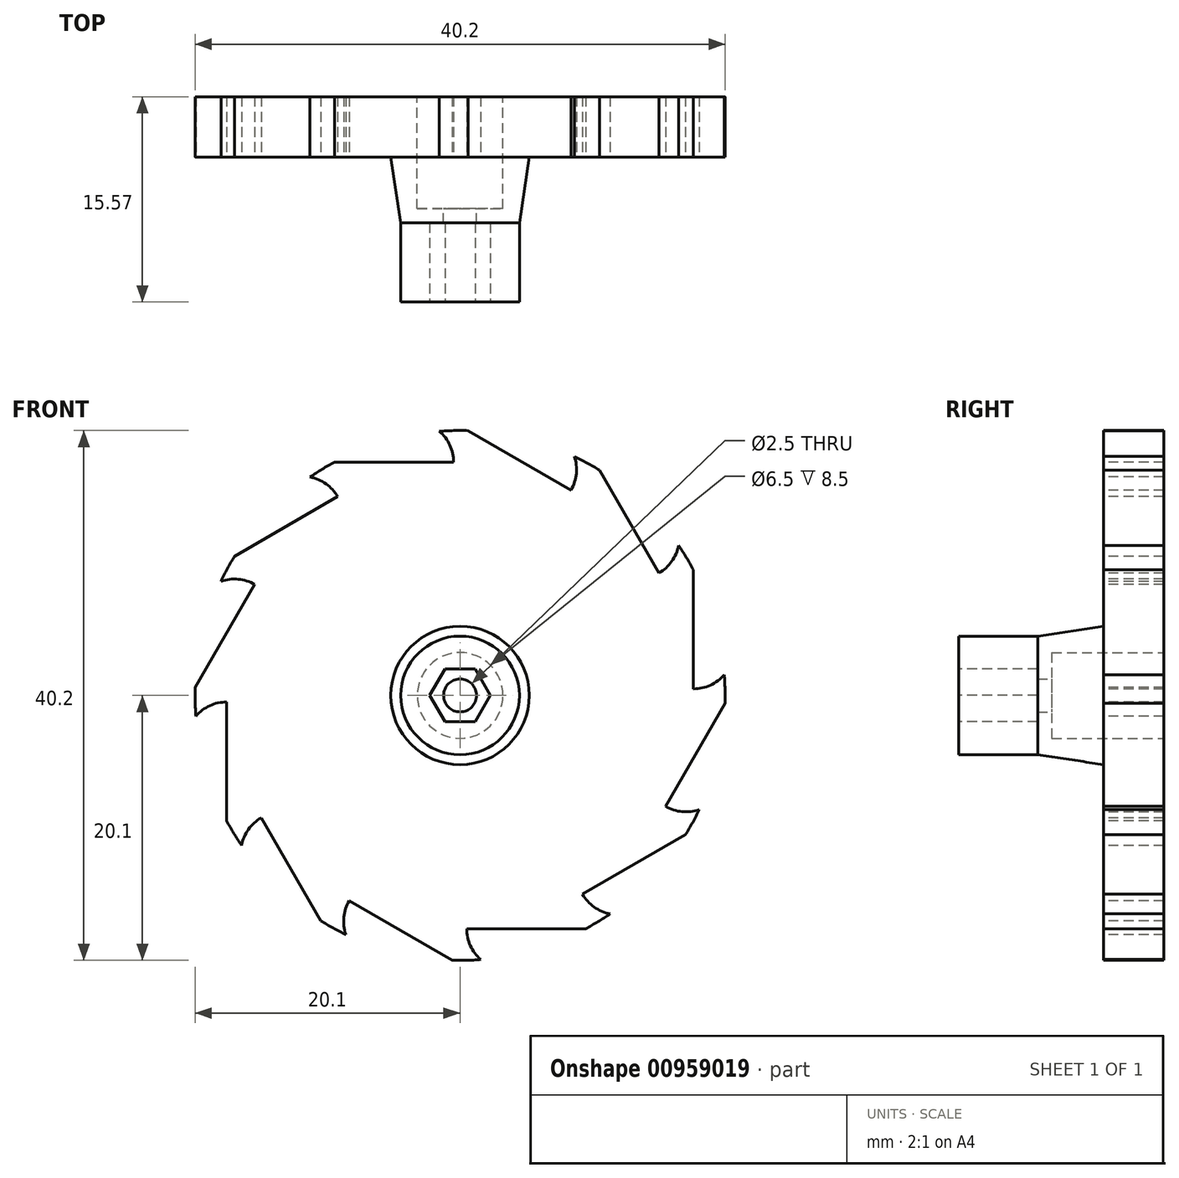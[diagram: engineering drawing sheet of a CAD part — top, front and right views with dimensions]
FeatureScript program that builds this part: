
annotation { "Feature Type Name" : "Feature", "Feature Type Description" : "" }
export const myFeature = defineFeature(function(context is Context, id is Id, definition is map)
    precondition{}
    {
        {
            var Q0;
            Q0=qCreatedBy(makeId("Front.planeOp"),FACE);
            var sketch = newSketch(context, id + "F0", { "sketchPlane" : qUnion([Q0])});
            skCircle(sketch, "E0", {"center": v(0, 0) * mm, "radius": 20.1 * mm});
            skSolve(sketch);
        }
        {
            var Q0;
            Q0=makeQuery(id+"F0.imprint","IMPRINT",FACE,{"disambiguationData":[TD([[makeQuery(id+"F0.imprint","IMPRINT",EDGE,{"derivedFrom":sQuery(id+"F0.wireOp",EDGE,"E0")}),1.0]])]});
            extrude(context, id + "F1", {"entities" : qUnion([Q0]), "depth" : 4.57 * mm, "offsetDistance" : 25.4 * mm});
        }
        {
            var Q0;
            Q0=makeQuery(id+"F1.opExtrude","CAP_FACE",FACE,{"disambiguationData":[OSD([sQuery(id+"F0.wireOp",EDGE,"E0")])],"isStart":false});
            var sketch = newSketch(context, id + "F2", { "sketchPlane" : qUnion([Q0])});
            skLineSegment(sketch, "E1", {"start": v(0, 20.1) * mm, "end": v(0, -20.1) * mm});
            skLineSegment(sketch, "E2", {"start": v(-9.53, 17.7) * mm, "end": v(9.53, 17.7) * mm});
            skArc(sketch, "E3", {"start": v(1.57, 20.04) * mm, "mid": v(0.78, 18.99) * mm, "end": v(0.5, 17.7) * mm});
            skArc(sketch, "E4.MirrorCS", {"start": v(-1.57, 20.04) * mm, "mid": v(-0.78, 18.99) * mm, "end": v(-0.5, 17.7) * mm});
            skArc(sketch, "E5", {"start": v(1.57, 20.04) * mm, "mid": v(0, 20.1) * mm, "end": v(-1.57, 20.04) * mm});
            skPoint(sketch, "E6.orphan", {"position": v(6.66, 17.7) * mm});
            skPoint(sketch, "E7.orphan", {"position": v(-6.66, 17.7) * mm});
            skSolve(sketch);
        }
        {
            var Q0;
            {var subQ5=sQuery(id+"F2.wireOp",EDGE,"E4.MirrorCS");Q0=makeQuery(id+"F2.imprint","IMPRINT",FACE,{"disambiguationData":[TD([[makeQuery(id+"F2.imprint","IMPRINT",EDGE,{"derivedFrom":subQ5}),1.0]])]});}
            var Q1;
            {var subQ5=sQuery(id+"F2.wireOp",EDGE,"E3");Q1=makeQuery(id+"F2.imprint","IMPRINT",FACE,{"disambiguationData":[TD([[makeQuery(id+"F2.imprint","IMPRINT",EDGE,{"derivedFrom":subQ5}),-1.0]])]});}
            extrude(context, id + "F3", {"entities" : qUnion([Q0, Q1]), "operationType" : NewBodyOperationType.REMOVE, "endBound" : BoundingType.THROUGH_ALL, "oppositeDirection" : true, "depth" : 25.4 * mm, "offsetDistance" : 25.4 * mm});
        }
        {
            var Q0;
            Q0=makeQuery(id+"F3.boolean.opBoolean","COPY",FACE,{"derivedFrom":makeQuery(id+"F3.opExtrude","SWEPT_FACE",FACE,{"disambiguationData":[OSD([sQuery(id+"F2.wireOp",EDGE,"E4.MirrorCS")])]})});
            var Q1;
            Q1=makeQuery(id+"F3.boolean.opBoolean","COPY",FACE,{"derivedFrom":makeQuery(id+"F3.opExtrude","SWEPT_FACE",FACE,{"disambiguationData":[OSD([sQuery(id+"F2.wireOp",EDGE,"E2")])]})});
            var Q2;
            Q2=makeQuery(id+"F3.boolean.opBoolean","COPY",FACE,{"derivedFrom":makeQuery(id+"F3.opExtrude","SWEPT_FACE",FACE,{"disambiguationData":[OSD([sQuery(id+"F2.wireOp",EDGE,"E3")])]})});
            var Q3;
            Q3=makeQuery(id+"F1.opExtrude","SWEPT_FACE",FACE,{"disambiguationData":[OSD([sQuery(id+"F0.wireOp",EDGE,"E0")])]});
            circularPattern(context, id + "F4", {"patternType" : PatternType.FACE, "faces" : qUnion([Q0, Q1, Q2]), "axis" : qUnion([Q3]), "angle" : 360 * degree, "instanceCount" : 36, "equalSpace" : true});
        }
        {
            var Q0;
            Q0=makeQuery(id+"F1.opExtrude","CAP_FACE",FACE,{"disambiguationData":[OSD([sQuery(id+"F0.wireOp",EDGE,"E0")])],"isStart":false});
            var sketch = newSketch(context, id + "F5", { "sketchPlane" : qUnion([Q0])});
            skCircle(sketch, "E8.cCircle", {"center": v(0, 0) * mm, "radius": 2 * mm, "construction": true});
            skLineSegment(sketch, "E8.0", {"start": v(-1.15, 2) * mm, "end": v(1.15, 2) * mm, "construction": true});
            skLineSegment(sketch, "E8.1", {"start": v(1.15, 2) * mm, "end": v(2.3, 0) * mm, "construction": true});
            skLineSegment(sketch, "E8.2", {"start": v(2.3, 0) * mm, "end": v(1.15, -2) * mm, "construction": true});
            skLineSegment(sketch, "E8.3", {"start": v(1.15, -2) * mm, "end": v(-1.15, -2) * mm, "construction": true});
            skLineSegment(sketch, "E8.4", {"start": v(-1.15, -2) * mm, "end": v(-2.3, 0) * mm, "construction": true});
            skLineSegment(sketch, "E8.5", {"start": v(-2.3, 0) * mm, "end": v(-1.15, 2) * mm, "construction": true});
            skPoint(sketch, "E8.0.midPoint", {"position": v(0, 2) * mm});
            skCircle(sketch, "E9", {"center": v(0, 0) * mm, "radius": 5.25 * mm});
            skSolve(sketch);
        }
        {
            var Q0;
            Q0=makeQuery(id+"F5.imprint","IMPRINT",FACE,{"disambiguationData":[TD([[makeQuery(id+"F5.imprint","IMPRINT",EDGE,{"derivedFrom":sQuery(id+"F5.wireOp",EDGE,"E9")}),-1.0]])]});
            cPlane(context, id + "F6", {"entities" : qUnion([Q0]), "cplaneType" : CPlaneType.OFFSET, "offset" : 5 * mm, "width" : 152.4 * mm, "height" : 152.4 * mm});
        }
        {
            var Q0;
            Q0=qCreatedBy(id+"F6.planeOp",FACE);
            var sketch = newSketch(context, id + "F7", { "sketchPlane" : qUnion([Q0])});
            skCircle(sketch, "E10.cCircle", {"center": v(0, 0) * mm, "radius": 2 * mm, "construction": true});
            skLineSegment(sketch, "E10.0", {"start": v(-1.15, 2) * mm, "end": v(1.15, 2) * mm, "construction": true});
            skLineSegment(sketch, "E10.1", {"start": v(1.15, 2) * mm, "end": v(2.3, 0) * mm, "construction": true});
            skLineSegment(sketch, "E10.2", {"start": v(2.3, 0) * mm, "end": v(1.15, -2) * mm, "construction": true});
            skLineSegment(sketch, "E10.3", {"start": v(1.15, -2) * mm, "end": v(-1.15, -2) * mm, "construction": true});
            skLineSegment(sketch, "E10.4", {"start": v(-1.15, -2) * mm, "end": v(-2.3, 0) * mm, "construction": true});
            skLineSegment(sketch, "E10.5", {"start": v(-2.3, 0) * mm, "end": v(-1.15, 2) * mm, "construction": true});
            skPoint(sketch, "E10.0.midPoint", {"position": v(0, 2) * mm});
            skCircle(sketch, "E11", {"center": v(0, 0) * mm, "radius": 4.5 * mm});
            skSolve(sketch);
        }
        {
            var Q1;
            Q1=makeQuery(id+"F5.imprint","IMPRINT",FACE,{"disambiguationData":[TD([[makeQuery(id+"F5.imprint","IMPRINT",EDGE,{"derivedFrom":sQuery(id+"F5.wireOp",EDGE,"E9")}),1.0]])]});
            var Q2;
            Q2=makeQuery(id+"F7.imprint","IMPRINT",FACE,{"disambiguationData":[TD([[makeQuery(id+"F7.imprint","IMPRINT",EDGE,{"derivedFrom":sQuery(id+"F7.wireOp",EDGE,"E11")}),1.0]])]});
            loft(context, id + "F8", {"operationType" : NewBodyOperationType.ADD, "sheetProfilesArray" : [{ "sheetProfileEntities" : qUnion([Q1]) }, { "sheetProfileEntities" : qUnion([Q2]) }]});
        }
        {
            var Q0;
            Q0=makeQuery(id+"F7.imprint","IMPRINT",FACE,{"disambiguationData":[TD([[makeQuery(id+"F7.imprint","IMPRINT",EDGE,{"derivedFrom":sQuery(id+"F7.wireOp",EDGE,"E11")}),1.0]])]});
            extrude(context, id + "F9", {"entities" : qUnion([Q0]), "operationType" : NewBodyOperationType.ADD, "depth" : 6 * mm, "offsetDistance" : 25.4 * mm});
        }
        {
            var Q0;
            Q0=makeQuery(id+"F1.opExtrude","CAP_FACE",FACE,{"disambiguationData":[OSD([sQuery(id+"F0.wireOp",EDGE,"E0")])],"isStart":true});
            var sketch = newSketch(context, id + "F10", { "sketchPlane" : qUnion([Q0])});
            skCircle(sketch, "E12", {"center": v(0, 0) * mm, "radius": 3.25 * mm});
            skSolve(sketch);
        }
        {
            var Q0;
            Q0=makeQuery(id+"F10.imprint","IMPRINT",FACE,{"disambiguationData":[TD([[makeQuery(id+"F10.imprint","IMPRINT",EDGE,{"derivedFrom":sQuery(id+"F10.wireOp",EDGE,"E12")}),1.0]])]});
            extrude(context, id + "F11", {"entities" : qUnion([Q0]), "operationType" : NewBodyOperationType.REMOVE, "oppositeDirection" : true, "depth" : 8.5 * mm, "offsetDistance" : 25.4 * mm});
        }
        {
            var Q0;
            Q0=makeQuery(id+"F11.boolean.opBoolean","COPY",FACE,{"derivedFrom":makeQuery(id+"F11.opExtrude","CAP_FACE",FACE,{"disambiguationData":[OSD([sQuery(id+"F10.wireOp",EDGE,"E12")])],"isStart":false})});
            var sketch = newSketch(context, id + "F12", { "sketchPlane" : qUnion([Q0])});
            skCircle(sketch, "E13", {"center": v(0, 0) * mm, "radius": 1.25 * mm});
            skSolve(sketch);
        }
        {
            var Q0;
            Q0=makeQuery(id+"F12.imprint","IMPRINT",FACE,{"disambiguationData":[TD([[makeQuery(id+"F12.imprint","IMPRINT",EDGE,{"derivedFrom":sQuery(id+"F12.wireOp",EDGE,"E13")}),1.0]])]});
            extrude(context, id + "F13", {"entities" : qUnion([Q0]), "operationType" : NewBodyOperationType.REMOVE, "endBound" : BoundingType.THROUGH_ALL, "oppositeDirection" : true, "depth" : 25.4 * mm, "offsetDistance" : 25.4 * mm});
        }
        {
            var Q0;
            Q0=makeQuery(id+"F9.opExtrude","CAP_FACE",FACE,{"disambiguationData":[OSD([sQuery(id+"F7.wireOp",EDGE,"E11")])],"isStart":false});
            var sketch = newSketch(context, id + "F14", { "sketchPlane" : qUnion([Q0])});
            skCircle(sketch, "E14.cCircle", {"center": v(0, 0) * mm, "radius": 2 * mm, "construction": true});
            skLineSegment(sketch, "E14.0", {"start": v(-1.15, 2) * mm, "end": v(1.15, 2) * mm});
            skLineSegment(sketch, "E14.1", {"start": v(1.15, 2) * mm, "end": v(2.3, 0) * mm});
            skLineSegment(sketch, "E14.2", {"start": v(2.3, 0) * mm, "end": v(1.15, -2) * mm});
            skLineSegment(sketch, "E14.3", {"start": v(1.15, -2) * mm, "end": v(-1.15, -2) * mm});
            skLineSegment(sketch, "E14.4", {"start": v(-1.15, -2) * mm, "end": v(-2.3, 0) * mm});
            skLineSegment(sketch, "E14.5", {"start": v(-2.3, 0) * mm, "end": v(-1.15, 2) * mm});
            skPoint(sketch, "E14.0.midPoint", {"position": v(0, 2) * mm});
            skSolve(sketch);
        }
        {
            var Q0;
            Q0=makeQuery(id+"F14.imprint","IMPRINT",FACE,{"disambiguationData":[TD([[makeQuery(id+"F14.imprint","IMPRINT",EDGE,{"derivedFrom":sQuery(id+"F14.wireOp",EDGE,"E14.0")}),-1.0]])]});
            extrude(context, id + "F15", {"entities" : qUnion([Q0]), "operationType" : NewBodyOperationType.REMOVE, "oppositeDirection" : true, "depth" : 6 * mm, "offsetDistance" : 25.4 * mm});
        }
    });
